# Revit family: JOMA_403, 404 & 405
name_source: partatom
category: Structural Connections
revit_build: Autodesk Revit Structure 2012 (Build: 20110309_2315(x64)
units: mm (PartAtom-declared; Revit-internal decimal feet)

## types (3) — shared parameters
Länk Joma Dimensioneringsverktyg = http://www.joma.se
Material = Varmförzinkad stålplåt
h = 90 mm  [stored 0.295276 ft]
l = 48 mm  [stored 0.15748 ft]
t = 3 mm  [stored 0.00984252 ft]
zero-valued in all types: Default Elevation

## per-type parameters (varying)
| type | Typ | Vikt | Vinkelbeslag 403 | Vinkelbeslag 404 | Vinkelbeslag 405 | b |
| 4040000 | VINKEL 404 | 0,202 | No | Yes | No | 76 mm  [stored 0.249344 ft] |
| 4030000 | VINKEL 403 | 0,132 | Yes | No | No | 48 mm  [stored 0.15748 ft] |
| 4050000 | VINKEL 405 | 0,316 | No | No | Yes | 116 mm  [stored 0.380577 ft] |

note: [stored X ft] marks values corroborated as IEEE doubles in the binary element streams (Revit-internal decimal feet)

## geometry (parser evidence)
native form markers: Sweep x3
no freeform markers — native parametric forms only
